# Revit family: Скамейка стальная «Лукс» Арт 12978
name_source: partatom
category: Антураж
revit_build: Autodesk Revit 2018 (Build: 20180423_1000(x64)
units: mm (PartAtom-declared; Revit-internal decimal feet)

## family parameters
Всегда вертикально = Да
Источник визуального образа = Геометрия семейства
На основе рабочей плоскости = Нет
Общий = Нет
При загрузке вырезать с полостями = Нет
Точка расчета площади = Нет

## types (4) — shared parameters
URL = https://hobbyka.ru
Артикул товара = Арт. 12978
Высота = 800 мм
Группа модели = Садовые скамейки
Изготовитель = ООО «Хоббика»
Изображение типоразмера = Скамейка стальная «Лукс» Арт 12978.jpg
Цвет опоры = Сталь
Ширина = 650 мм

## per-type parameters (varying)
| type | Версия 1,5 м | Версия 1,5 м (композит) | Версия 1,8 м | Версия 1,8 м (композит) | Длина | Материал изделия | Описание | Цвет сидения |
| Версия 1,5 м | Да | Нет | Нет | Нет | 1500 мм | Сталь, дерево | Скамейка стальная «Лукс». Версия 1,5 м | Сосна |
| Версия 1,8 м | Нет | Нет | Да | Нет | 1800 мм | Сталь, дерево | Скамейка стальная «Лукс». Версия 1,8 м | Сосна |
| Версия 1,5 м (композит) | Нет | Да | Нет | Нет | 1500 мм | Сталь, композитные материалы | Скамейка стальная «Лукс». Версия 1,5 м (композит) | Композитные материалы |
| Версия 1,8 м (композит) | Нет | Нет | Нет | Да | 1800 мм | Сталь, композитные материалы | Скамейка стальная «Лукс». Версия 1,8 м (композит) | Композитные материалы |
